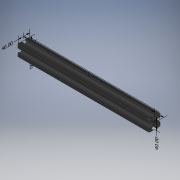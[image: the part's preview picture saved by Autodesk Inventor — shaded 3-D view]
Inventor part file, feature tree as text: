
AUTODESK INVENTOR PART (.ipt)
format: ipt  version: 2019 (Build 230136000, 136)  size: 274,944 bytes
history: native  units: mm
features: other x125, extrude x1, sketch x1
ambient origin geometry x8: Origin, YZ Plane, XZ Plane, XY Plane, X Axis, Y Axis, Z Axis, Center Point
bodies: Solid1 (feature_tree)
feature tree (127):
  other  "Annotations"
  extrude  "Extrusion1"  [1 undecoded]
  other  "CS_ANBAU_HINTEN_LINKS_XY"
  other  "CS_ANBAU_HINTEN_LINKS_YZ"
  other  "CS_ANBAU_HINTEN_LINKS_ZX"
  other  "CS_ANBAU_HINTEN_LINKS_X"
  other  "CS_ANBAU_HINTEN_LINKS_Y"
  other  "CS_ANBAU_HINTEN_LINKS_Z"
  other  "CS_ANBAU_HINTEN_LINKS_Center"
  other  "CS_ANBAU_HINTEN_OBEN_XY"
  other  "CS_ANBAU_HINTEN_OBEN_YZ"
  other  "CS_ANBAU_HINTEN_OBEN_ZX"
  other  "CS_ANBAU_HINTEN_OBEN_X"
  other  "CS_ANBAU_HINTEN_OBEN_Y"
  other  "CS_ANBAU_HINTEN_OBEN_Z"
  other  "CS_ANBAU_HINTEN_OBEN_Center"
  other  "CS_ANBAU_HINTEN_RECHTS_XY"
  other  "CS_ANBAU_HINTEN_RECHTS_YZ"
  other  "CS_ANBAU_HINTEN_RECHTS_ZX"
  other  "CS_ANBAU_HINTEN_RECHTS_X"
  other  "CS_ANBAU_HINTEN_RECHTS_Y"
  other  "CS_ANBAU_HINTEN_RECHTS_Z"
  other  "CS_ANBAU_HINTEN_RECHTS_Center"
  other  "CS_ANBAU_HINTEN_UNTEN_XY"
  other  "CS_ANBAU_HINTEN_UNTEN_YZ"
  other  "CS_ANBAU_HINTEN_UNTEN_ZX"
  other  "CS_ANBAU_HINTEN_UNTEN_X"
  other  "CS_ANBAU_HINTEN_UNTEN_Y"
  other  "CS_ANBAU_HINTEN_UNTEN_Z"
  other  "CS_ANBAU_HINTEN_UNTEN_Center"
  other  "CS_ANBAU_QUER_XY"
  other  "CS_ANBAU_QUER_YZ"
  other  "CS_ANBAU_QUER_ZX"
  other  "CS_ANBAU_QUER_X"
  other  "CS_ANBAU_QUER_Y"
  other  "CS_ANBAU_QUER_Z"
  other  "CS_ANBAU_QUER_Center"
  other  "CS_ANBAU_QUER_1_XY"
  other  "CS_ANBAU_QUER_1_YZ"
  other  "CS_ANBAU_QUER_1_ZX"
  other  "CS_ANBAU_QUER_1_X"
  other  "CS_ANBAU_QUER_1_Y"
  other  "CS_ANBAU_QUER_1_Z"
  other  "CS_ANBAU_QUER_1_Center"
  other  "CS_ANBAU_VORNE_LINKS_XY"
  other  "CS_ANBAU_VORNE_LINKS_YZ"
  other  "CS_ANBAU_VORNE_LINKS_ZX"
  other  "CS_ANBAU_VORNE_LINKS_X"
  other  "CS_ANBAU_VORNE_LINKS_Y"
  other  "CS_ANBAU_VORNE_LINKS_Z"
  other  "CS_ANBAU_VORNE_LINKS_Center"
  other  "CS_ANBAU_VORNE_OBEN_XY"
  other  "CS_ANBAU_VORNE_OBEN_YZ"
  other  "CS_ANBAU_VORNE_OBEN_ZX"
  other  "CS_ANBAU_VORNE_OBEN_X"
  other  "CS_ANBAU_VORNE_OBEN_Y"
  other  "CS_ANBAU_VORNE_OBEN_Z"
  other  "CS_ANBAU_VORNE_OBEN_Center"
  other  "CS_ANBAU_VORNE_RECHTS_XY"
  other  "CS_ANBAU_VORNE_RECHTS_YZ"
  other  "CS_ANBAU_VORNE_RECHTS_ZX"
  other  "CS_ANBAU_VORNE_RECHTS_X"
  other  "CS_ANBAU_VORNE_RECHTS_Y"
  other  "CS_ANBAU_VORNE_RECHTS_Z"
  other  "CS_ANBAU_VORNE_RECHTS_Center"
  other  "CS_ANBAU_VORNE_UNTEN_XY"
  other  "CS_ANBAU_VORNE_UNTEN_YZ"
  other  "CS_ANBAU_VORNE_UNTEN_ZX"
  other  "CS_ANBAU_VORNE_UNTEN_X"
  other  "CS_ANBAU_VORNE_UNTEN_Y"
  other  "CS_ANBAU_VORNE_UNTEN_Z"
  other  "CS_ANBAU_VORNE_UNTEN_Center"
  other  "p1_XY"
  other  "p1_YZ"
  other  "p1_ZX"
  other  "p1_X"
  other  "p1_Y"
  other  "p1_Z"
  other  "p1_Center"
  other  "p2_XY"
  other  "p2_YZ"
  other  "p2_ZX"
  other  "p2_X"
  other  "p2_Y"
  other  "p2_Z"
  other  "p2_Center"
  other  "p3_XY"
  other  "p3_YZ"
  other  "p3_ZX"
  other  "p3_X"
  other  "p3_Y"
  other  "p3_Z"
  other  "p3_Center"
  other  "p4_XY"
  other  "p4_YZ"
  other  "p4_ZX"
  other  "p4_X"
  other  "p4_Y"
  other  "p4_Z"
  other  "p4_Center"
  other  "p5_XY"
  other  "p5_YZ"
  other  "p5_ZX"
  other  "p5_X"
  other  "p5_Y"
  other  "p5_Z"
  other  "p5_Center"
  other  "pm1_XY"
  other  "pm1_YZ"
  other  "pm1_ZX"
  other  "pm1_X"
  other  "pm1_Y"
  other  "pm1_Z"
  other  "pm1_Center"
  other  "pm2_XY"
  other  "pm2_YZ"
  other  "pm2_ZX"
  other  "pm2_X"
  other  "pm2_Y"
  other  "pm2_Z"
  other  "pm2_Center"
  sketch  "Skizze_1"  dims[d0=456.0mm d1=0.0mm d2=0.0mm d3=0.0mm d4=0.0mm d5=0.0mm d6=0.0mm d10=456.0mm d11=456.0mm d7=40.0mm d8=40.0mm d9=40.0mm]
  other  "Linear Dimension 1"
  other  "Linear Dimension 2"
  other  "Linear Dimension 3"
  other  "Linear Dimension 4"
  other  "Linear Dimension 5"
note: 1 required parameter value undecoded (feature->parameter linkage not recoverable at this tier; creation-order binding heuristic only, values carry confidence <= 0.55)
